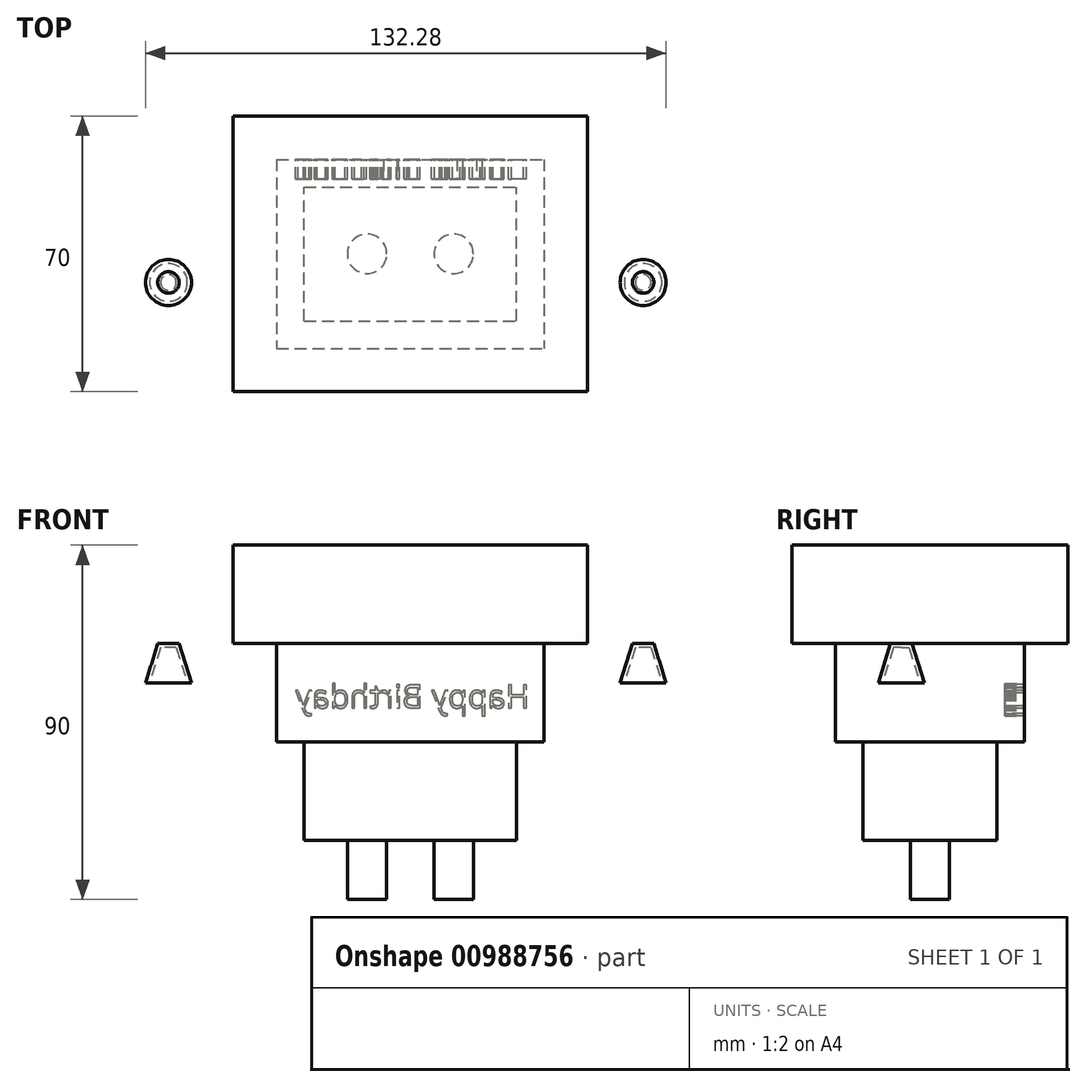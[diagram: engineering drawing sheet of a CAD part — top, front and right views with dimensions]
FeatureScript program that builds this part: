
annotation { "Feature Type Name" : "Feature", "Feature Type Description" : "" }
export const myFeature = defineFeature(function(context is Context, id is Id, definition is map)
    precondition{}
    {
        {
            var Q0;
            Q0=qCreatedBy(makeId("Top.planeOp"),FACE);
            var sketch = newSketch(context, id + "F0", { "sketchPlane" : qUnion([Q0])});
            skLineSegment(sketch, "E0.bottom", {"start": v(-43.85, -27.74) * mm, "end": v(46.15, -27.74) * mm});
            skLineSegment(sketch, "E0.top", {"start": v(-43.85, 42.26) * mm, "end": v(46.15, 42.26) * mm});
            skLineSegment(sketch, "E0.left", {"start": v(-43.85, -27.74) * mm, "end": v(-43.85, 42.26) * mm});
            skLineSegment(sketch, "E0.right", {"start": v(46.15, -27.74) * mm, "end": v(46.15, 42.26) * mm});
            skSolve(sketch);
        }
        {
            var Q0;
            Q0 = qSketchRegion(id + "F0", true);
            extrude(context, id + "F1", {"entities" : qUnion([Q0]), "depth" : 25 * mm, "offsetDistance" : 25 * mm});
        }
        {
            var Q0;
            Q0=makeQuery(id+"F1.opExtrude","CAP_FACE",FACE,{"disambiguationData":[OSD([sQuery(id+"F0.wireOp",EDGE,"E0.bottom"),sQuery(id+"F0.wireOp",EDGE,"E0.top"),sQuery(id+"F0.wireOp",EDGE,"E0.left"),sQuery(id+"F0.wireOp",EDGE,"E0.right")])],"isStart":true});
            var sketch = newSketch(context, id + "F2", { "sketchPlane" : qUnion([Q0])});
            skLineSegment(sketch, "E1.bottom", {"start": v(-32.85, -31.26) * mm, "end": v(35.15, -31.26) * mm});
            skLineSegment(sketch, "E1.top", {"start": v(-32.85, 16.74) * mm, "end": v(35.15, 16.74) * mm});
            skLineSegment(sketch, "E1.left", {"start": v(-32.85, -31.26) * mm, "end": v(-32.85, 16.74) * mm});
            skLineSegment(sketch, "E1.right", {"start": v(35.15, -31.26) * mm, "end": v(35.15, 16.74) * mm});
            skSolve(sketch);
        }
        {
            var Q0;
            Q0 = qSketchRegion(id + "F2", true);
            extrude(context, id + "F3", {"entities" : qUnion([Q0]), "operationType" : NewBodyOperationType.ADD, "depth" : 25 * mm, "offsetDistance" : 25 * mm});
        }
        {
            var Q0;
            Q0=makeQuery(id+"F3.opExtrude","CAP_FACE",FACE,{"disambiguationData":[OSD([sQuery(id+"F2.wireOp",EDGE,"E1.bottom"),sQuery(id+"F2.wireOp",EDGE,"E1.top"),sQuery(id+"F2.wireOp",EDGE,"E1.left"),sQuery(id+"F2.wireOp",EDGE,"E1.right")])],"isStart":false});
            var sketch = newSketch(context, id + "F4", { "sketchPlane" : qUnion([Q0])});
            skLineSegment(sketch, "E2.bottom", {"start": v(-25.85, 9.74) * mm, "end": v(28.15, 9.74) * mm});
            skLineSegment(sketch, "E2.top", {"start": v(-25.85, -24.26) * mm, "end": v(28.15, -24.26) * mm});
            skLineSegment(sketch, "E2.left", {"start": v(-25.85, 9.74) * mm, "end": v(-25.85, -24.26) * mm});
            skLineSegment(sketch, "E2.right", {"start": v(28.15, 9.74) * mm, "end": v(28.15, -24.26) * mm});
            skSolve(sketch);
        }
        {
            var Q0;
            Q0 = qSketchRegion(id + "F4", true);
            extrude(context, id + "F5", {"entities" : qUnion([Q0]), "operationType" : NewBodyOperationType.ADD, "depth" : 25 * mm, "offsetDistance" : 25 * mm});
        }
        {
            var Q0;
            Q0=makeQuery(id+"F5.opExtrude","CAP_FACE",FACE,{"disambiguationData":[OSD([sQuery(id+"F4.wireOp",EDGE,"E2.bottom"),sQuery(id+"F4.wireOp",EDGE,"E2.top"),sQuery(id+"F4.wireOp",EDGE,"E2.left"),sQuery(id+"F4.wireOp",EDGE,"E2.right")])],"isStart":false});
            var sketch = newSketch(context, id + "F6", { "sketchPlane" : qUnion([Q0])});
            skCircle(sketch, "E3", {"center": v(-9.85, -7.26) * mm, "radius": 5 * mm});
            skPoint(sketch, "E3.centerSnap0", {"position": v(-25.85, -7.26) * mm});
            skCircle(sketch, "E4", {"center": v(12.15, -7.26) * mm, "radius": 5 * mm});
            skSolve(sketch);
        }
        {
            var Q0;
            Q0 = qSketchRegion(id + "F6", true);
            extrude(context, id + "F7", {"entities" : qUnion([Q0]), "operationType" : NewBodyOperationType.ADD, "depth" : 15 * mm, "offsetDistance" : 25 * mm});
        }
        {
            var Q0;
            Q0=makeQuery(id+"F3.opExtrude","SWEPT_FACE",FACE,{"disambiguationData":[OSD([sQuery(id+"F2.wireOp",EDGE,"E1.bottom")])]});
            var sketch = newSketch(context, id + "F8", { "sketchPlane" : qUnion([Q0])});
            skText(sketch, "E5", { "text": "Happy Birthday", "fontName": "OpenSans-Regular.ttf"});
            const initialGuessF8  = {"E5": [-0.03141, -0.01637, 1, 0, 0.00592]};
            skSetInitialGuess(sketch, initialGuessF8);
            skSolve(sketch);
        }
        {
            var Q0;
            Q0 = qSketchRegion(id + "F8", true);
            extrude(context, id + "F9", {"entities" : qUnion([Q0]), "operationType" : NewBodyOperationType.REMOVE, "oppositeDirection" : true, "depth" : 5 * mm, "offsetDistance" : 25 * mm});
        }
        {
            var Q0;
            Q0=qCreatedBy(makeId("Front.planeOp"),FACE);
            var sketch = newSketch(context, id + "F10", { "sketchPlane" : qUnion([Q0])});
            skLineSegment(sketch, "E6", {"start": v(63.03, 0) * mm, "end": v(66.14, -10.06) * mm});
            skLineSegment(sketch, "E7", {"start": v(66.14, -10.06) * mm, "end": v(60.3, -10.06) * mm});
            skLineSegment(sketch, "E8", {"start": v(60.3, -10.06) * mm, "end": v(60.3, 0) * mm});
            skLineSegment(sketch, "E9", {"start": v(60.3, 0) * mm, "end": v(63.03, 0) * mm});
            skLineSegment(sketch, "E10", {"start": v(60.3, -13.13) * mm, "end": v(60.3, -16.33) * mm});
            skSolve(sketch);
        }
        {
            var Q0;
            Q0=makeQuery(id+"F10.imprint","IMPRINT",FACE,{"disambiguationData":[TD([[makeQuery(id+"F10.imprint","IMPRINT",EDGE,{"derivedFrom":sQuery(id+"F10.wireOp",EDGE,"E6")}),-1.0]])]});
            var Q1;
            Q1=sQuery(id+"F10.wireOp",EDGE,"E10");
            revolve(context, id + "F11", {"surfaceOperationType" : NewSurfaceOperationType.NEW, "entities" : qUnion([Q0]), "axis" : qUnion([Q1]), "revolveType" : RevolveType.FULL});
        }
        {
            var Q0;
            Q0=makeQuery(id+"F11.opRevolve","SWEPT_FACE",FACE,{"disambiguationData":[OSD([sQuery(id+"F10.wireOp",EDGE,"E7")])]});
            shell(context, id + "F12", {"entities" : qUnion([Q0]), "thickness" : 1 * mm});
        }
        {
            var Q0;
            Q0=makeQuery(id+"F11.opRevolve","SWEPT_BODY",BODY,{"disambiguationData":[OSD([sQuery(id+"F10.wireOp",EDGE,"E6"),sQuery(id+"F10.wireOp",EDGE,"E7"),sQuery(id+"F10.wireOp",EDGE,"E8"),sQuery(id+"F10.wireOp",EDGE,"E9")])]});
            var Q1;
            Q1=qCreatedBy(makeId("Right.planeOp"),FACE);
            mirror(context, id + "F13", {"entities" : qUnion([Q0]), "mirrorPlane" : qUnion([Q1])});
        }
    });
